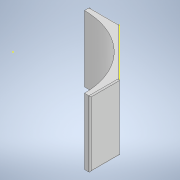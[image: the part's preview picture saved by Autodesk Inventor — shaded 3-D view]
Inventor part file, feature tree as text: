
AUTODESK INVENTOR PART (.ipt)
format: ipt  version: 2021 (Build 250183000, 183)  size: 197,120 bytes
history: native  units: mm
features: sketch x3, extrude x2, other x1, fillet x1
ambient origin geometry x8: Origin, YZ Plane, XZ Plane, XY Plane, X Axis, Y Axis, Z Axis, Center Point
bodies: Body1 (feature_tree)
feature tree (7):
  other  "Sólido1"
  extrude  "Extrusión1"  Depth=2.5mm
  sketch  "Boceto2"  dims[d19=0.5mm d20=1.0mm d21=0.0mm]
  fillet  "Empalme1"  Radius=30.0mm
  extrude  "Extrusión3"  Depth=1.0mm TaperAngle=0.0deg
  sketch  "Boceto1"  dims[d2=2.5mm d3=2.5mm d4=30.0mm d5=0.0mm]
  sketch  "Boceto9"  dims[d6=0.5mm d7=0.872665mm d22=0.5mm d23=0.872665mm]
